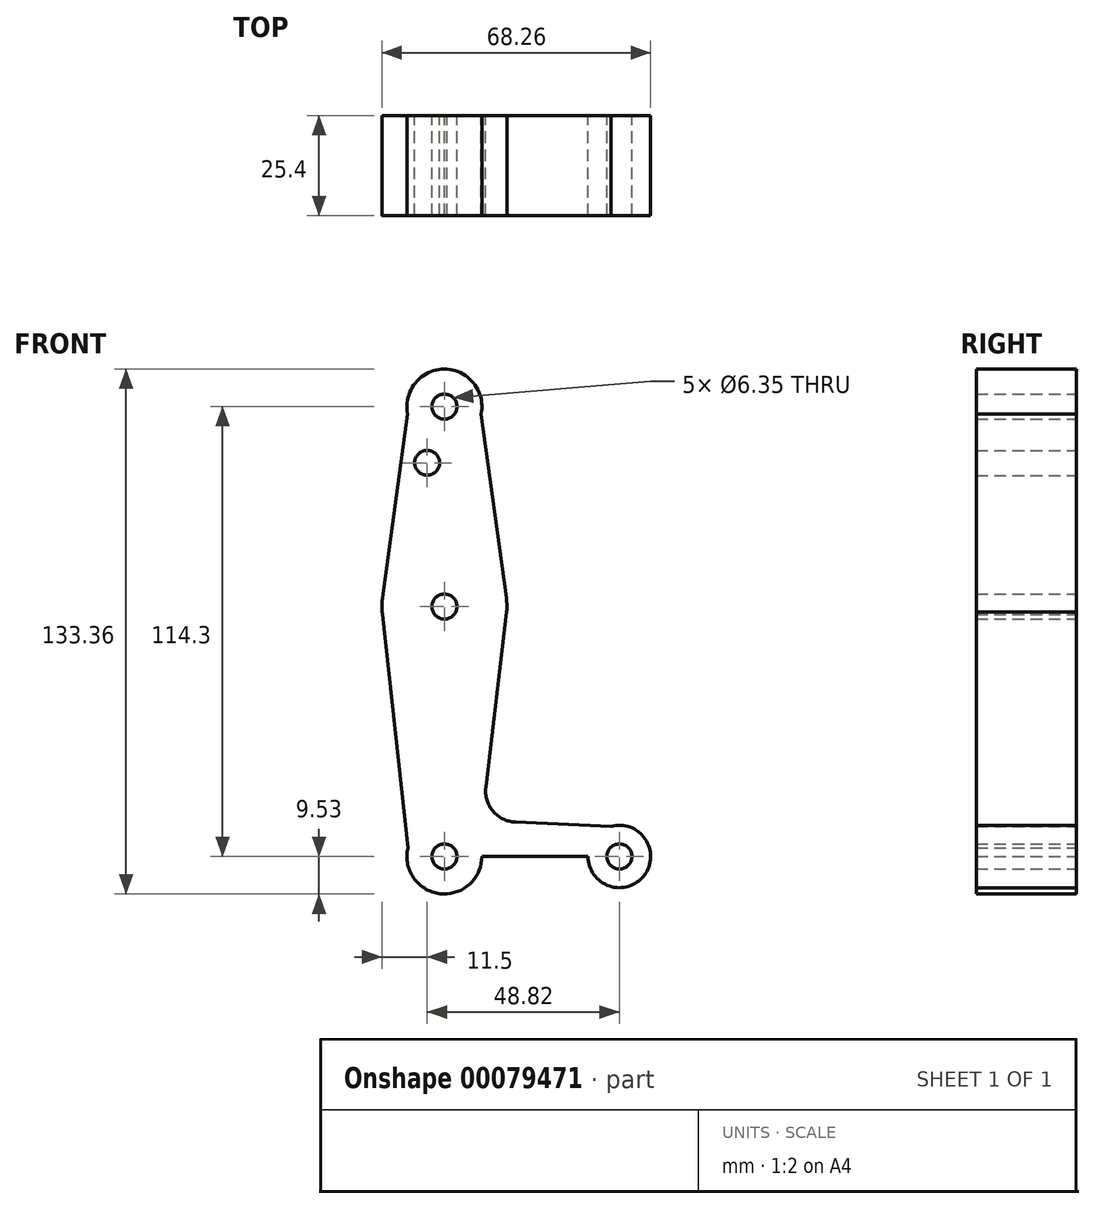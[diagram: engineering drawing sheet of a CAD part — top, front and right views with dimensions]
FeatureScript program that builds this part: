
annotation { "Feature Type Name" : "Feature", "Feature Type Description" : "" }
export const myFeature = defineFeature(function(context is Context, id is Id, definition is map)
    precondition{}
    {
        {
            var Q0;
            Q0=qCreatedBy(makeId("Front.planeOp"),FACE);
            var sketch = newSketch(context, id + "F0", { "sketchPlane" : qUnion([Q0])});
            skCircle(sketch, "E0", {"center": v(0, 0) * mm, "radius": 9.53 * mm});
            skCircle(sketch, "E1", {"center": v(0, 63.5) * mm, "radius": 15.88 * mm});
            skCircle(sketch, "E2", {"center": v(0, 114.3) * mm, "radius": 9.53 * mm});
            skLineSegment(sketch, "E3", {"start": v(44.45, 0) * mm, "end": v(0, 0) * mm});
            skLineSegment(sketch, "E4", {"start": v(0, 114.3) * mm, "end": v(0, 0) * mm});
            skCircle(sketch, "E5", {"center": v(44.45, 0) * mm, "radius": 7.94 * mm});
            skLineSegment(sketch, "E6", {"start": v(9.33, 112.4) * mm, "end": v(15.73, 65.65) * mm});
            skLineSegment(sketch, "E7", {"start": v(-9.33, 112.4) * mm, "end": v(-15.73, 65.65) * mm});
            skLineSegment(sketch, "E8", {"start": v(15.82, 62.17) * mm, "end": v(10.5, 17.6) * mm});
            skLineSegment(sketch, "E9", {"start": v(18.05, 8.72) * mm, "end": v(42.31, 7.64) * mm});
            skLineSegment(sketch, "E10", {"start": v(-15.75, 61.5) * mm, "end": v(-9.26, 2.23) * mm});
            skLineSegment(sketch, "E11", {"start": v(0, -9.53) * mm, "end": v(44.73, -7.93) * mm});
            skArc(sketch, "E12.filletArc", {"start": v(10.5, 17.6) * mm, "mid": v(12.34, 11.52) * mm, "end": v(18.05, 8.72) * mm});
            skCircle(sketch, "E13", {"center": v(0, 114.3) * mm, "radius": 3.18 * mm});
            skCircle(sketch, "E14", {"center": v(0, 63.5) * mm, "radius": 3.18 * mm});
            skCircle(sketch, "E15", {"center": v(0, 0) * mm, "radius": 3.18 * mm});
            skCircle(sketch, "E16", {"center": v(44.45, 0) * mm, "radius": 3.18 * mm});
            skCircle(sketch, "E17", {"center": v(-4.37, 100.03) * mm, "radius": 3.18 * mm});
            skSolve(sketch);
        }
        {
            var Q0;
            {var subQ5=sQuery(id+"F0.wireOp",EDGE,"E7");Q0=makeQuery(id+"F0.imprint","IMPRINT",FACE,{"disambiguationData":[TD([[makeQuery(id+"F0.imprint","IMPRINT",EDGE,{"derivedFrom":subQ5}),1.0]])]});}
            var Q1;
            {var subQ0=sQuery(id+"F0.wireOp",EDGE,"E6");Q1=makeQuery(id+"F0.imprint","IMPRINT",FACE,{"disambiguationData":[TD([[makeQuery(id+"F0.imprint","IMPRINT",EDGE,{"derivedFrom":subQ0}),-1.0]])]});}
            var Q2;
            Q2=makeQuery(id+"F0.imprint","IMPRINT",FACE,{"disambiguationData":[TD([[makeQuery(id+"F0.imprint","IMPRINT",EDGE,{"derivedFrom":sQuery(id+"F0.wireOp",EDGE,"E13")}),-1.0]])]});
            var Q3;
            {var subQ0=sQuery(id+"F0.wireOp",EDGE,"E1");var subQ8=makeQuery(id+"F0.imprint","INTERSECT",VERTEX,{"derivedFrom":[subQ0,sQuery(id+"F0.wireOp",EDGE,"E7")]});Q3=makeQuery(id+"F0.imprint","IMPRINT",FACE,{"disambiguationData":[TD([[makeQuery(id+"F0.imprint","IMPRINT",EDGE,{"disambiguationData":[TD([[subQ8,1.0]])],"derivedFrom":subQ0}),1.0]])]});}
            var Q4;
            {var subQ0=sQuery(id+"F0.wireOp",EDGE,"E1");var subQ1=makeQuery(id+"F0.imprint","INTERSECT",VERTEX,{"derivedFrom":[subQ0,sQuery(id+"F0.wireOp",EDGE,"E6")]});Q4=makeQuery(id+"F0.imprint","IMPRINT",FACE,{"disambiguationData":[TD([[makeQuery(id+"F0.imprint","IMPRINT",EDGE,{"disambiguationData":[TD([[subQ1,-1.0]])],"derivedFrom":subQ0}),1.0]])]});}
            var Q5;
            {var subQ0=sQuery(id+"F0.wireOp",EDGE,"E10");Q5=makeQuery(id+"F0.imprint","IMPRINT",FACE,{"disambiguationData":[TD([[makeQuery(id+"F0.imprint","IMPRINT",EDGE,{"derivedFrom":subQ0}),1.0]])]});}
            var Q6;
            {var subQ11=sQuery(id+"F0.wireOp",EDGE,"E9");Q6=makeQuery(id+"F0.imprint","IMPRINT",FACE,{"disambiguationData":[TD([[makeQuery(id+"F0.imprint","IMPRINT",EDGE,{"derivedFrom":subQ11}),-1.0]])]});}
            var Q7;
            {var subQ0=sQuery(id+"F0.wireOp",EDGE,"E11");var subQ1=sQuery(id+"F0.wireOp",EDGE,"E0");var subQ2=makeQuery(id+"F0.imprint","INTERSECT",VERTEX,{"disambiguationData":[OD(1.0)],"derivedFrom":[subQ1,subQ0]});Q7=makeQuery(id+"F0.imprint","IMPRINT",FACE,{"disambiguationData":[TD([[makeQuery(id+"F0.imprint","IMPRINT",EDGE,{"disambiguationData":[TD([[subQ2,-1.0]])],"derivedFrom":subQ1}),-1.0]])]});}
            var Q8;
            Q8=makeQuery(id+"F0.imprint","IMPRINT",FACE,{"disambiguationData":[TD([[makeQuery(id+"F0.imprint","IMPRINT",EDGE,{"derivedFrom":sQuery(id+"F0.wireOp",EDGE,"E16")}),-1.0]])]});
            var Q9;
            {var subQ1=sQuery(id+"F0.wireOp",EDGE,"E0");var subQ7=makeQuery(id+"F0.imprint","INTERSECT",VERTEX,{"derivedFrom":[subQ1,sQuery(id+"F0.wireOp",EDGE,"E10")]});Q9=makeQuery(id+"F0.imprint","IMPRINT",FACE,{"disambiguationData":[TD([[makeQuery(id+"F0.imprint","IMPRINT",EDGE,{"disambiguationData":[TD([[subQ7,1.0]])],"derivedFrom":subQ1}),1.0]])]});}
            var Q10;
            {var subQ0=sQuery(id+"F0.wireOp",EDGE,"E4");var subQ1=sQuery(id+"F0.wireOp",EDGE,"E0");var subQ2=makeQuery(id+"F0.imprint","INTERSECT",VERTEX,{"derivedFrom":[subQ1,subQ0]});Q10=makeQuery(id+"F0.imprint","IMPRINT",FACE,{"disambiguationData":[TD([[makeQuery(id+"F0.imprint","IMPRINT",EDGE,{"disambiguationData":[TD([[subQ2,1.0]])],"derivedFrom":subQ1}),1.0]])]});}
            extrude(context, id + "F1", {"entities" : qUnion([Q0, Q1, Q2, Q3, Q4, Q5, Q6, Q7, Q8, Q9, Q10]), "depth" : 25.4 * mm});
        }
    });
